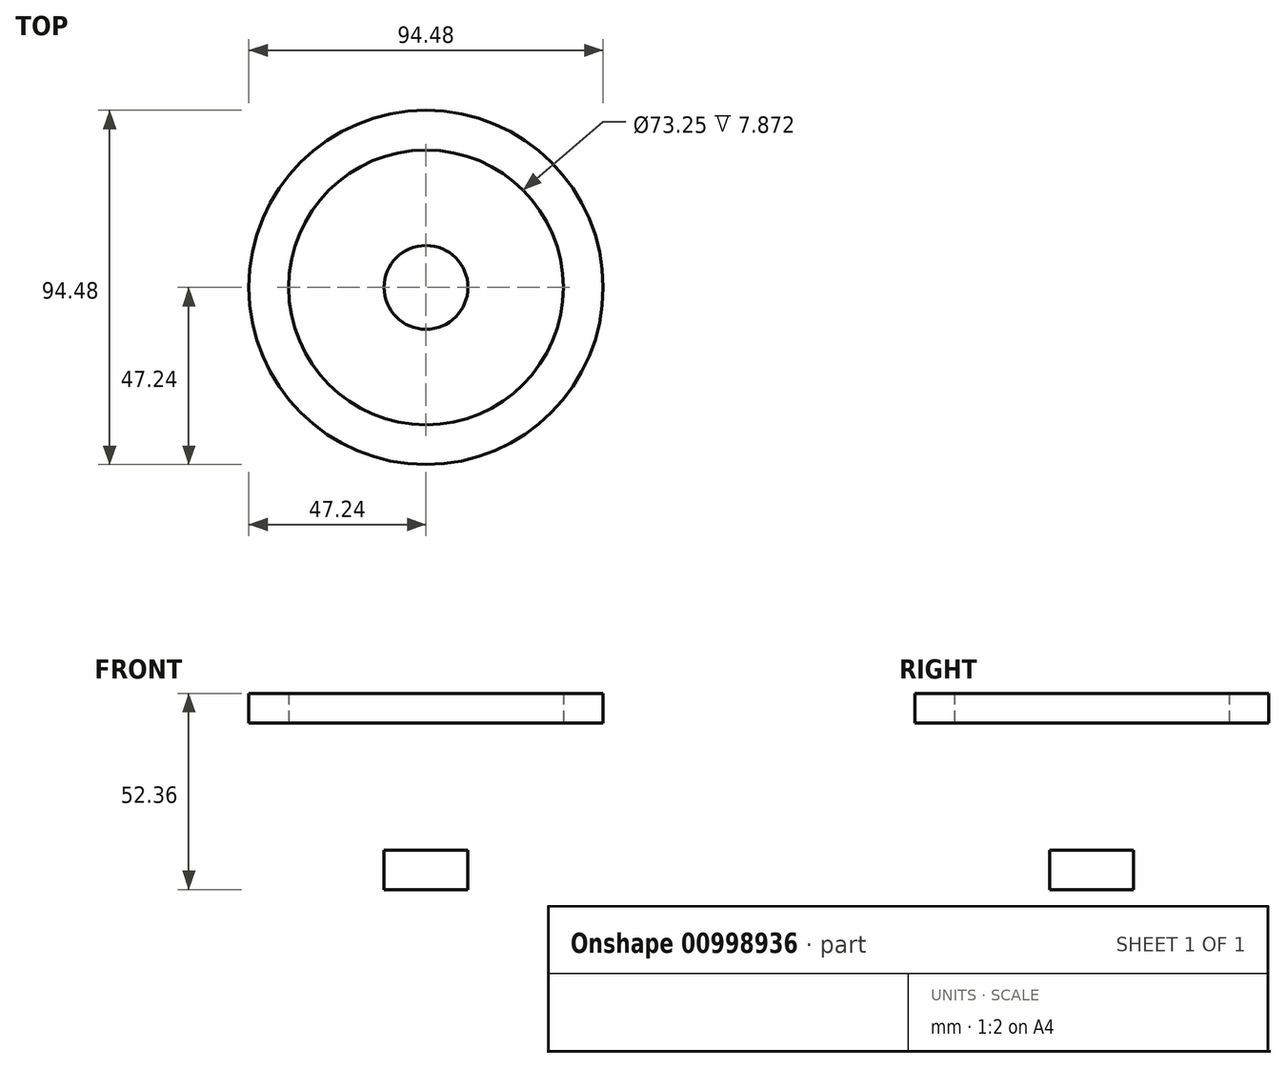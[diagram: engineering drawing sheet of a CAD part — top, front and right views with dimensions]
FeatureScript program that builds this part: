
annotation { "Feature Type Name" : "Feature", "Feature Type Description" : "" }
export const myFeature = defineFeature(function(context is Context, id is Id, definition is map)
    precondition{}
    {
        {
            var Q0;
            Q0=qCreatedBy(makeId("Front.planeOp"),FACE);
            var sketch = newSketch(context, id + "F0", { "sketchPlane" : qUnion([Q0])});
            skLineSegment(sketch, "E0.bottom", {"start": v(0, 0) * mm, "end": v(11.19, 0) * mm});
            skLineSegment(sketch, "E0.top", {"start": v(0, 10.53) * mm, "end": v(11.19, 10.53) * mm});
            skLineSegment(sketch, "E0.left", {"start": v(0, 0) * mm, "end": v(0, 10.53) * mm});
            skLineSegment(sketch, "E0.right", {"start": v(11.19, 0) * mm, "end": v(11.19, 10.53) * mm});
            skLineSegment(sketch, "E1.bottom", {"start": v(36.63, 52.36) * mm, "end": v(47.24, 52.36) * mm});
            skLineSegment(sketch, "E1.top", {"start": v(36.63, 44.48) * mm, "end": v(47.24, 44.48) * mm});
            skLineSegment(sketch, "E1.left", {"start": v(36.63, 52.36) * mm, "end": v(36.63, 44.48) * mm});
            skLineSegment(sketch, "E1.right", {"start": v(47.24, 52.36) * mm, "end": v(47.24, 44.48) * mm});
            skLineSegment(sketch, "E2", {"start": v(0, 0) * mm, "end": v(0, 100.62) * mm, "construction": true});
            skSolve(sketch);
        }
        {
            var Q0;
            Q0=makeQuery(id+"F0.imprint","IMPRINT",FACE,{"disambiguationData":[TD([[makeQuery(id+"F0.imprint","IMPRINT",EDGE,{"derivedFrom":sQuery(id+"F0.wireOp",EDGE,"E0.bottom")}),1.0]])]});
            var Q1;
            Q1=makeQuery(id+"F0.imprint","IMPRINT",FACE,{"disambiguationData":[TD([[makeQuery(id+"F0.imprint","IMPRINT",EDGE,{"derivedFrom":sQuery(id+"F0.wireOp",EDGE,"E1.bottom")}),-1.0]])]});
            var Q2;
            Q2=sQuery(id+"F0.wireOp",EDGE,"E2");
            revolve(context, id + "F1", {"surfaceOperationType" : NewSurfaceOperationType.NEW, "entities" : qUnion([Q0, Q1]), "axis" : qUnion([Q2]), "revolveType" : RevolveType.FULL});
        }
    });
